# Revit family: PipeFitting_Elbow_WallPlate_PressWater-B_Conex_Female
name_source: partatom
category: Pipe Fittings
units: mm (PartAtom-declared; Revit-internal decimal feet)

## family parameters
Always vertical = Yes
Cut with Voids When Loaded = No
OmniClass Number = 23.60.30.11.14
OmniClass Title = Pipework Fittings
Part Type = Elbow
Round Connector Dimension = Use Radius
Shared = No
Work Plane-Based = No

## types (1)
- Standard_WallplateElbow
    Assembly Code = D2090800
    Lookup Table Name = Elbow_Wall Plate_PressWater-B_Conex_FEMALE
    Manufacturer = Conex | Bänninger
    Material = <By Category>
    Model = Standard_WallplateElbow
    Model Specification = BMA
    Model Version = 2013-03
    NATSPECWorkSection = TBC
    OmniclassProducts = TBC
    Type Comments = Conex Bänninger specialises in providing the best plumbing fittings and accessories across the globe by offering innovative and versatile jointing solutions. Since 1909 Conex Bänninger has produced over 10 billion copper fittings and has built its reputation for quality manufacturing, back by first-class customer service and unrivalled expertise. Passionate about excellence, Conex Bänninger is a byword for quality in the domestic, commercial, industrial, air conditioning and refrigeration markets worldwide.
Conex Bänninger is an ISO 9000 quality assured company, which assures you the very best in quality.
Conex Bänninger >B< Press is a versatile press fitting system for use with hard, half hard or soft copper tube providing a secure, life long, leak-proof joint.
Approved Tools - The following tools are approved tools for installation of >B< Press fittings:
•	Romax compact (Rothenberger)
•	Romax 3000 (Rothenberger)
•	Picco (Viega)
•	PT3-AH & 4B (Viega)
    URL = http://www.conexbanninger.com.au
    Uniformat IIElements = TBC

## geometry (parser evidence)
native form markers: Sweep x3
no freeform markers — native parametric forms only
